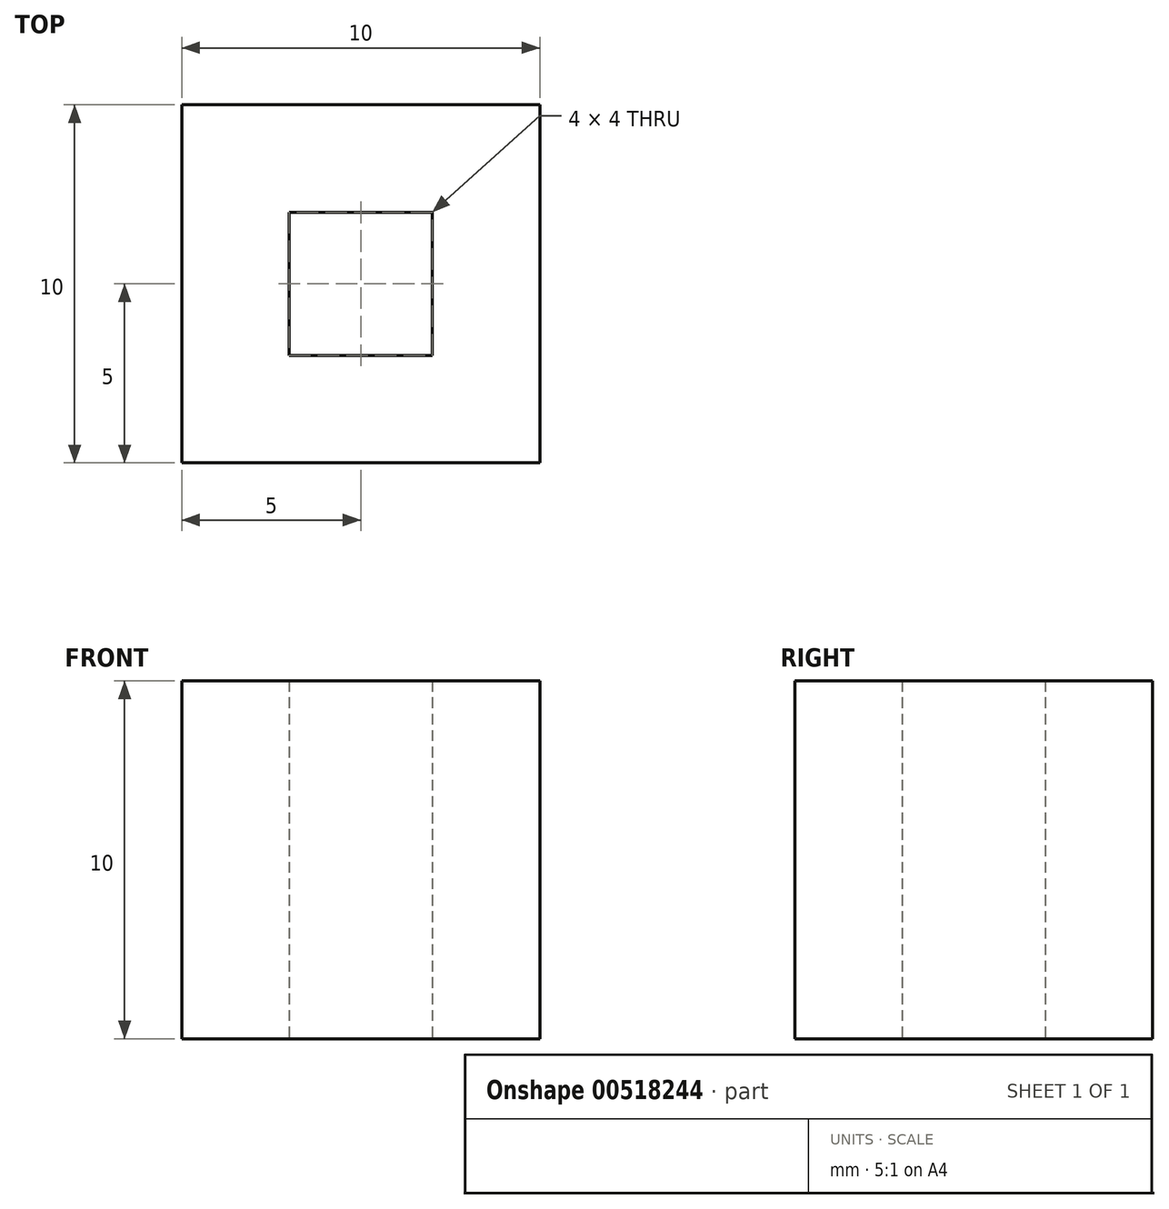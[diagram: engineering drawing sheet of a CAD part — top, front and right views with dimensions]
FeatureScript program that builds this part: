
annotation { "Feature Type Name" : "Feature", "Feature Type Description" : "" }
export const myFeature = defineFeature(function(context is Context, id is Id, definition is map)
    precondition{}
    {
        {
            var Q0;
            Q0=qCreatedBy(makeId("Top.planeOp"),FACE);
            var sketch = newSketch(context, id + "F0", { "sketchPlane" : qUnion([Q0])});
            skLineSegment(sketch, "E0.bottom", {"start": v(-5, 5) * mm, "end": v(5, 5) * mm});
            skLineSegment(sketch, "E0.top", {"start": v(-5, -5) * mm, "end": v(5, -5) * mm});
            skLineSegment(sketch, "E0.left", {"start": v(-5, 5) * mm, "end": v(-5, -5) * mm});
            skLineSegment(sketch, "E0.right", {"start": v(5, 5) * mm, "end": v(5, -5) * mm});
            skLineSegment(sketch, "E1", {"start": v(-5, 0) * mm, "end": v(5, 0) * mm, "construction": true});
            skLineSegment(sketch, "E2.0", {"start": v(-2, 2) * mm, "end": v(2, 2) * mm});
            skLineSegment(sketch, "E3.0", {"start": v(2, 2) * mm, "end": v(2, -2) * mm});
            skLineSegment(sketch, "E4.0", {"start": v(-2, -2) * mm, "end": v(2, -2) * mm});
            skLineSegment(sketch, "E5.0", {"start": v(-2, 2) * mm, "end": v(-2, -2) * mm});
            skSolve(sketch);
        }
        {
            var Q0;
            Q0 = qSketchRegion(id + "F0", true);
            extrude(context, id + "F1", {"entities" : qUnion([Q0]), "depth" : 10 * mm, "offsetDistance" : 25 * mm});
        }
    });
